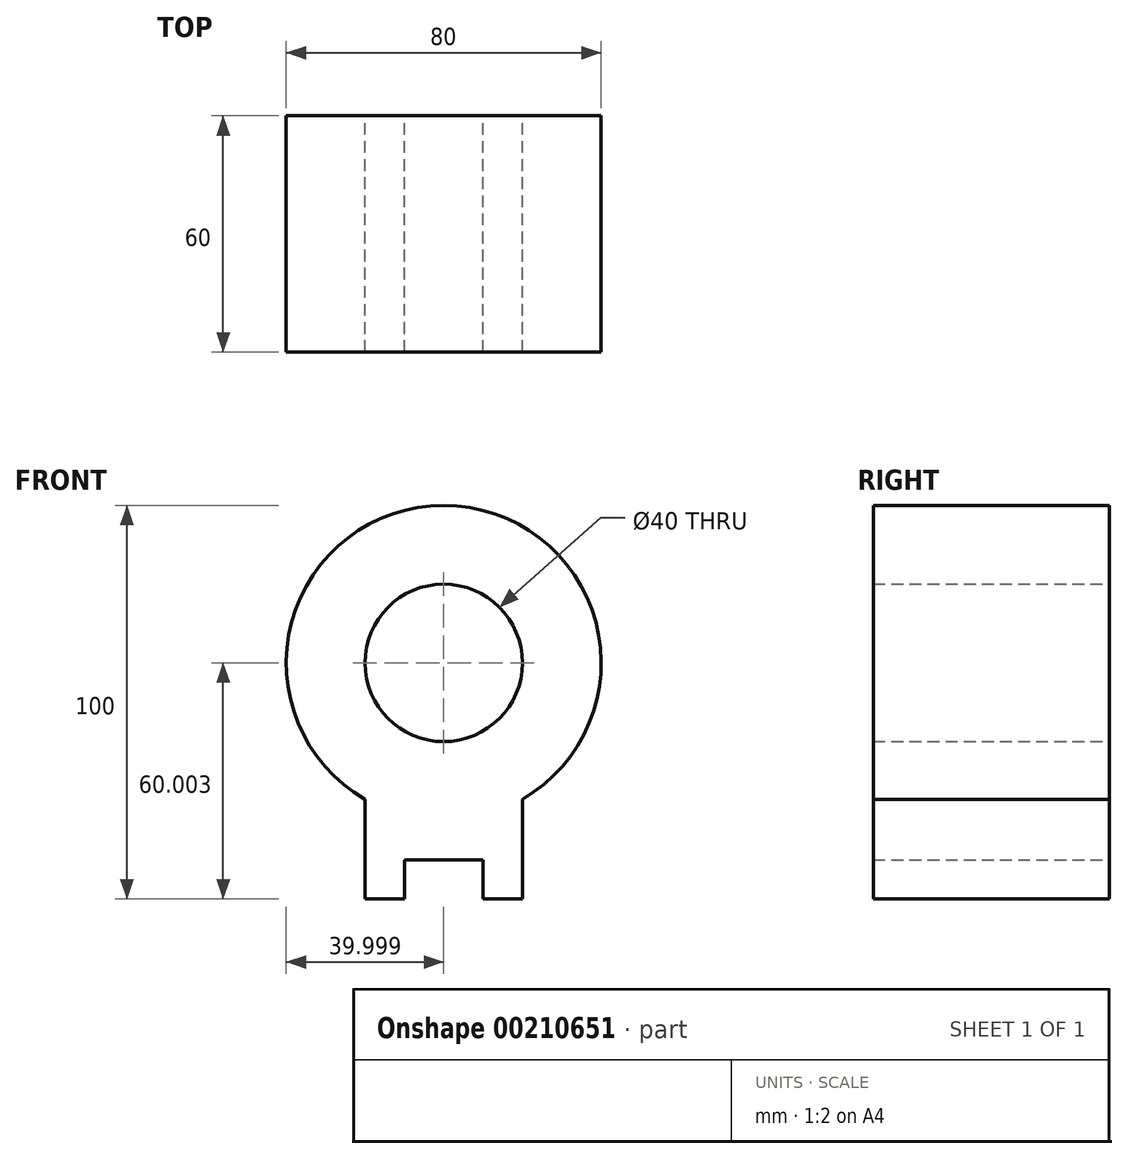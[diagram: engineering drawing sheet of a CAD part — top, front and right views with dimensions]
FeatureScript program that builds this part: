
annotation { "Feature Type Name" : "Feature", "Feature Type Description" : "" }
export const myFeature = defineFeature(function(context is Context, id is Id, definition is map)
    precondition{}
    {
        {
            var Q0;
            Q0=qCreatedBy(makeId("Front.planeOp"),FACE);
            var sketch = newSketch(context, id + "F0", { "sketchPlane" : qUnion([Q0])});
            skLineSegment(sketch, "E0", {"start": v(-51.45, -43.45) * mm, "end": v(-41.45, -43.45) * mm});
            skLineSegment(sketch, "E1", {"start": v(-41.45, -43.45) * mm, "end": v(-41.45, -33.45) * mm});
            skLineSegment(sketch, "E2", {"start": v(-41.45, -33.45) * mm, "end": v(-21.45, -33.45) * mm});
            skLineSegment(sketch, "E3", {"start": v(-21.45, -33.45) * mm, "end": v(-21.45, -43.45) * mm});
            skLineSegment(sketch, "E4", {"start": v(-21.45, -43.45) * mm, "end": v(-11.45, -43.45) * mm});
            skLineSegment(sketch, "E5", {"start": v(-11.45, -43.45) * mm, "end": v(-11.45, -23.45) * mm});
            skLineSegment(sketch, "E6", {"start": v(-51.45, -43.45) * mm, "end": v(-51.45, -23.45) * mm});
            skLineSegment(sketch, "E7", {"start": v(-51.45, -23.45) * mm, "end": v(-51.45, -18.09) * mm});
            skLineSegment(sketch, "E8", {"start": v(-11.45, -23.45) * mm, "end": v(-11.45, -18.09) * mm});
            skArc(sketch, "E9", {"start": v(-51.45, -18.09) * mm, "mid": v(-31.45, 56.55) * mm, "end": v(-11.45, -18.09) * mm});
            skCircle(sketch, "E10", {"center": v(-31.45, 16.55) * mm, "radius": 20 * mm});
            skSolve(sketch);
        }
        {
            var Q0;
            Q0=makeQuery(id+"F0.imprint","IMPRINT",FACE,{"disambiguationData":[TD([[makeQuery(id+"F0.imprint","IMPRINT",EDGE,{"derivedFrom":sQuery(id+"F0.wireOp",EDGE,"E0")}),1.0]])]});
            extrude(context, id + "F1", {"entities" : qUnion([Q0]), "depth" : 60 * mm});
        }
    });
